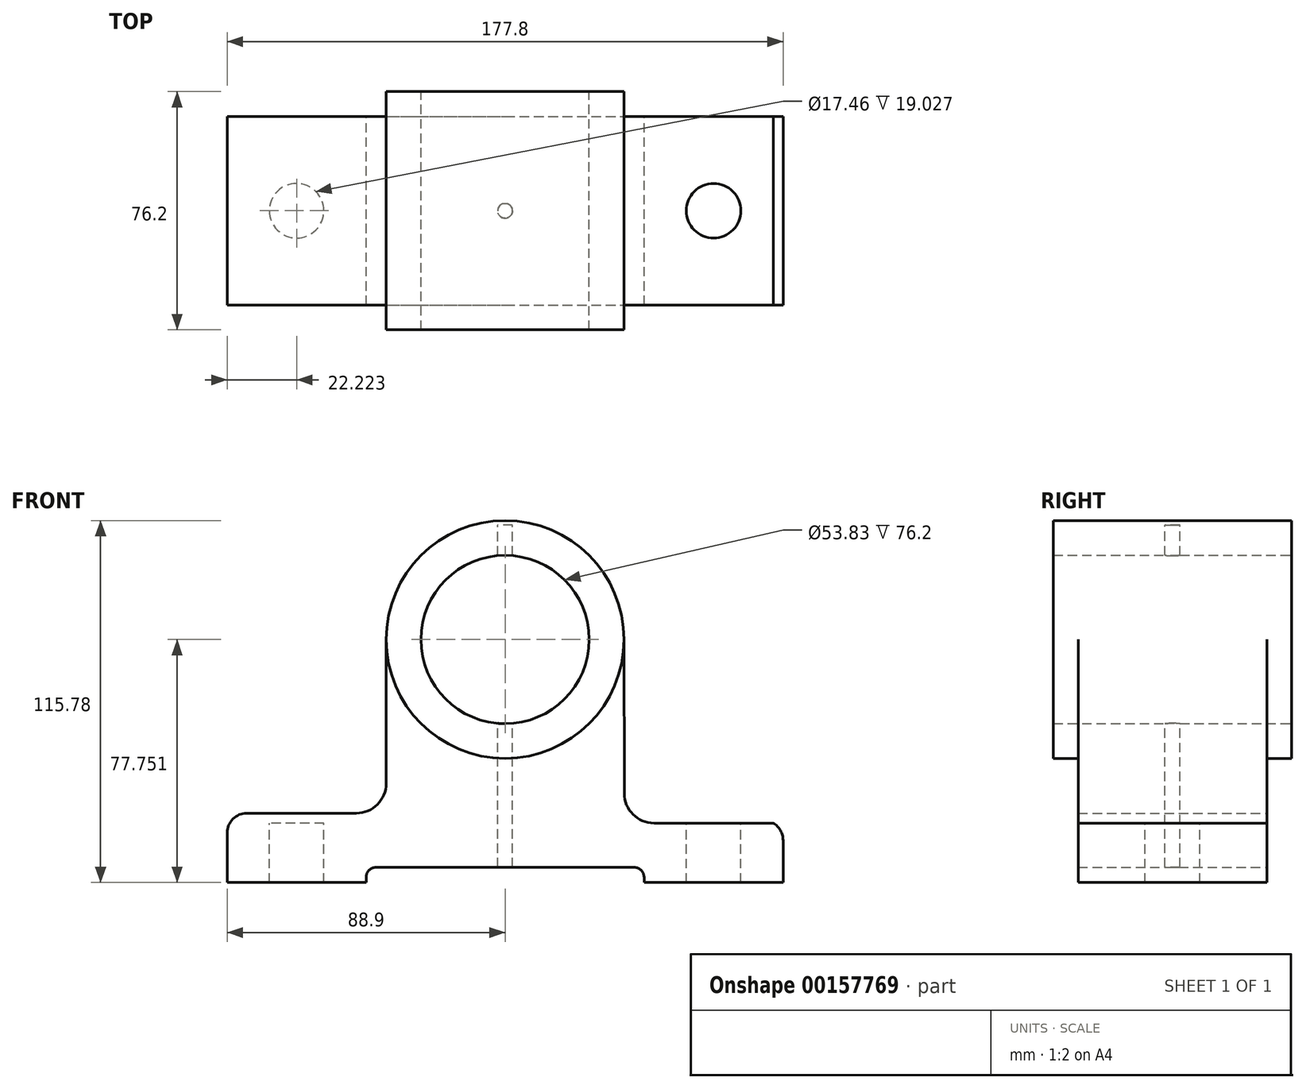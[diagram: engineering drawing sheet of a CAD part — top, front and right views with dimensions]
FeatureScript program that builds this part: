
annotation { "Feature Type Name" : "Feature", "Feature Type Description" : "" }
export const myFeature = defineFeature(function(context is Context, id is Id, definition is map)
    precondition{}
    {
        {
            var Q0;
            Q0=qCreatedBy(makeId("Front.planeOp"),FACE);
            var sketch = newSketch(context, id + "F0", { "sketchPlane" : qUnion([Q0])});
            skLineSegment(sketch, "E0", {"start": v(44.45, 1.7) * mm, "end": v(44.45, 0) * mm});
            skLineSegment(sketch, "E1", {"start": v(-44.45, 1.7) * mm, "end": v(-44.45, 0) * mm});
            skLineSegment(sketch, "E2", {"start": v(-88.9, 0) * mm, "end": v(-44.45, 0) * mm});
            skLineSegment(sketch, "E3", {"start": v(44.45, 0) * mm, "end": v(88.9, 0) * mm});
            skLineSegment(sketch, "E4", {"start": v(-41.27, 4.87) * mm, "end": v(41.28, 4.87) * mm});
            skLineSegment(sketch, "E5", {"start": v(88.9, 0) * mm, "end": v(88.9, 13.53) * mm});
            skLineSegment(sketch, "E6", {"start": v(-88.9, 0) * mm, "end": v(-88.9, 15.85) * mm});
            skPoint(sketch, "E7.endSnap0", {"position": v(0, 4.87) * mm});
            skCircle(sketch, "E8", {"center": v(0, 77.75) * mm, "radius": 26.92 * mm});
            skCircle(sketch, "E9", {"center": v(0, 77.75) * mm, "radius": 38.03 * mm});
            skLineSegment(sketch, "E10", {"start": v(-82.55, 22.2) * mm, "end": v(-47.55, 22.2) * mm});
            skLineSegment(sketch, "E11", {"start": v(-38.03, 77.75) * mm, "end": v(-38.03, 31.72) * mm});
            skPoint(sketch, "E12.visualSharp", {"position": v(-88.9, 22.2) * mm});
            skArc(sketch, "E12.filletArc", {"start": v(-82.55, 22.2) * mm, "mid": v(-87.04, 20.34) * mm, "end": v(-88.9, 15.85) * mm});
            skPoint(sketch, "E13.visualSharp", {"position": v(88.9, 22.2) * mm});
            skArc(sketch, "E13.filletArc", {"start": v(88.9, 13.53) * mm, "mid": v(88.05, 16.7) * mm, "end": v(85.72, 19.03) * mm});
            skPoint(sketch, "E14.visualSharp", {"position": v(-44.45, 4.87) * mm});
            skArc(sketch, "E14.filletArc", {"start": v(-41.27, 4.87) * mm, "mid": v(-43.52, 3.94) * mm, "end": v(-44.45, 1.7) * mm});
            skPoint(sketch, "E15.visualSharp", {"position": v(44.45, 4.87) * mm});
            skArc(sketch, "E15.filletArc", {"start": v(44.45, 1.7) * mm, "mid": v(43.52, 3.94) * mm, "end": v(41.28, 4.87) * mm});
            skLineSegment(sketch, "E16", {"start": v(38.03, 77.75) * mm, "end": v(38.1, 28.54) * mm});
            skLineSegment(sketch, "E17", {"start": v(85.72, 19.03) * mm, "end": v(47.63, 19.03) * mm});
            skPoint(sketch, "E18.visualSharp", {"position": v(38.12, 19.03) * mm});
            skArc(sketch, "E18.filletArc", {"start": v(38.1, 28.54) * mm, "mid": v(40.9, 21.81) * mm, "end": v(47.63, 19.03) * mm});
            skPoint(sketch, "E19.visualSharp", {"position": v(-38.03, 22.2) * mm});
            skArc(sketch, "E19.filletArc", {"start": v(-47.55, 22.2) * mm, "mid": v(-40.82, 24.99) * mm, "end": v(-38.03, 31.72) * mm});
            skSolve(sketch);
        }
        {
            var Q0;
            Q0=makeQuery(id+"F0.imprint","IMPRINT",FACE,{"disambiguationData":[TD([[makeQuery(id+"F0.imprint","IMPRINT",EDGE,{"derivedFrom":sQuery(id+"F0.wireOp",EDGE,"E0")}),1.0]])]});
            extrude(context, id + "F1", {"entities" : qUnion([Q0]), "endBound" : BoundingType.SYMMETRIC, "depth" : 60.32 * mm});
        }
        {
            var Q0;
            Q0=makeQuery(id+"F0.imprint","IMPRINT",FACE,{"disambiguationData":[TD([[makeQuery(id+"F0.imprint","IMPRINT",EDGE,{"derivedFrom":sQuery(id+"F0.wireOp",EDGE,"E8")}),-1.0]])]});
            extrude(context, id + "F2", {"entities" : qUnion([Q0]), "operationType" : NewBodyOperationType.ADD, "endBound" : BoundingType.SYMMETRIC, "depth" : 76.2 * mm});
        }
        {
            var Q0;
            Q0=makeQuery(id+"F1.opExtrude","SWEPT_FACE",FACE,{"disambiguationData":[OSD([sQuery(id+"F0.wireOp",EDGE,"E17")])]});
            var sketch = newSketch(context, id + "F3", { "sketchPlane" : qUnion([Q0])});
            skPoint(sketch, "E20.endSnap0", {"position": v(47.63, 0) * mm});
            skPoint(sketch, "E21", {"position": v(-66.68, 0) * mm});
            skPoint(sketch, "E22", {"position": v(66.68, 0) * mm});
            skSolve(sketch);
        }
        {
            var Q0;
            Q0=qCreatedBy(makeId("Top.planeOp"),FACE);
            cPlane(context, id + "F4", {"entities" : qUnion([Q0]), "cplaneType" : CPlaneType.OFFSET, "offset" : 114.3 * mm, "width" : 152.4 * mm, "height" : 152.4 * mm});
        }
        {
            var Q0;
            Q0=qCreatedBy(id+"F4.planeOp",FACE);
            var sketch = newSketch(context, id + "F5", { "sketchPlane" : qUnion([Q0])});
            skPoint(sketch, "E23", {"position": v(0, 0) * mm});
            skSolve(sketch);
        }
        {
            var Q0;
            Q0=sQuery(id+"F5.wireOp",VERTEX,"E23");
            var Q1;
            Q1=makeQuery(id+"F1.opExtrude","SWEPT_BODY",BODY,{"disambiguationData":[OSD([sQuery(id+"F0.wireOp",EDGE,"E0"),sQuery(id+"F0.wireOp",EDGE,"E1"),sQuery(id+"F0.wireOp",EDGE,"E2"),sQuery(id+"F0.wireOp",EDGE,"E3"),sQuery(id+"F0.wireOp",EDGE,"E4"),sQuery(id+"F0.wireOp",EDGE,"E5"),sQuery(id+"F0.wireOp",EDGE,"E6"),sQuery(id+"F0.wireOp",EDGE,"E9"),sQuery(id+"F0.wireOp",EDGE,"E10"),sQuery(id+"F0.wireOp",EDGE,"E11"),sQuery(id+"F0.wireOp",EDGE,"E12.filletArc"),sQuery(id+"F0.wireOp",EDGE,"E13.filletArc"),sQuery(id+"F0.wireOp",EDGE,"E14.filletArc"),sQuery(id+"F0.wireOp",EDGE,"E15.filletArc"),sQuery(id+"F0.wireOp",EDGE,"E16"),sQuery(id+"F0.wireOp",EDGE,"E17"),sQuery(id+"F0.wireOp",EDGE,"E18.filletArc"),sQuery(id+"F0.wireOp",EDGE,"E19.filletArc")])]});
            hole(context, id + "F6", {"style" : HoleStyle.SIMPLE, "endStyle" : HoleEndStyle.THROUGH, "holeDiameter" : 4.76 * mm, "locations" : qUnion([Q0]), "scope" : qUnion([Q1]), "isTappedThrough" : true});
        }
        {
            var Q0;
            Q0=sQuery(id+"F3.wireOp",VERTEX,"E21");
            var Q1;
            Q1=sQuery(id+"F3.wireOp",VERTEX,"E22");
            var Q2;
            Q2=makeQuery(id+"F1.opExtrude","SWEPT_BODY",BODY,{"disambiguationData":[OSD([sQuery(id+"F0.wireOp",EDGE,"E0"),sQuery(id+"F0.wireOp",EDGE,"E1"),sQuery(id+"F0.wireOp",EDGE,"E2"),sQuery(id+"F0.wireOp",EDGE,"E3"),sQuery(id+"F0.wireOp",EDGE,"E4"),sQuery(id+"F0.wireOp",EDGE,"E5"),sQuery(id+"F0.wireOp",EDGE,"E6"),sQuery(id+"F0.wireOp",EDGE,"E9"),sQuery(id+"F0.wireOp",EDGE,"E10"),sQuery(id+"F0.wireOp",EDGE,"E11"),sQuery(id+"F0.wireOp",EDGE,"E12.filletArc"),sQuery(id+"F0.wireOp",EDGE,"E13.filletArc"),sQuery(id+"F0.wireOp",EDGE,"E14.filletArc"),sQuery(id+"F0.wireOp",EDGE,"E15.filletArc"),sQuery(id+"F0.wireOp",EDGE,"E16"),sQuery(id+"F0.wireOp",EDGE,"E17"),sQuery(id+"F0.wireOp",EDGE,"E18.filletArc"),sQuery(id+"F0.wireOp",EDGE,"E19.filletArc")])]});
            hole(context, id + "F7", {"style" : HoleStyle.SIMPLE, "endStyle" : HoleEndStyle.THROUGH, "holeDiameter" : 17.46 * mm, "locations" : qUnion([Q0, Q1]), "scope" : qUnion([Q2]), "isTappedThrough" : true});
        }
    });
